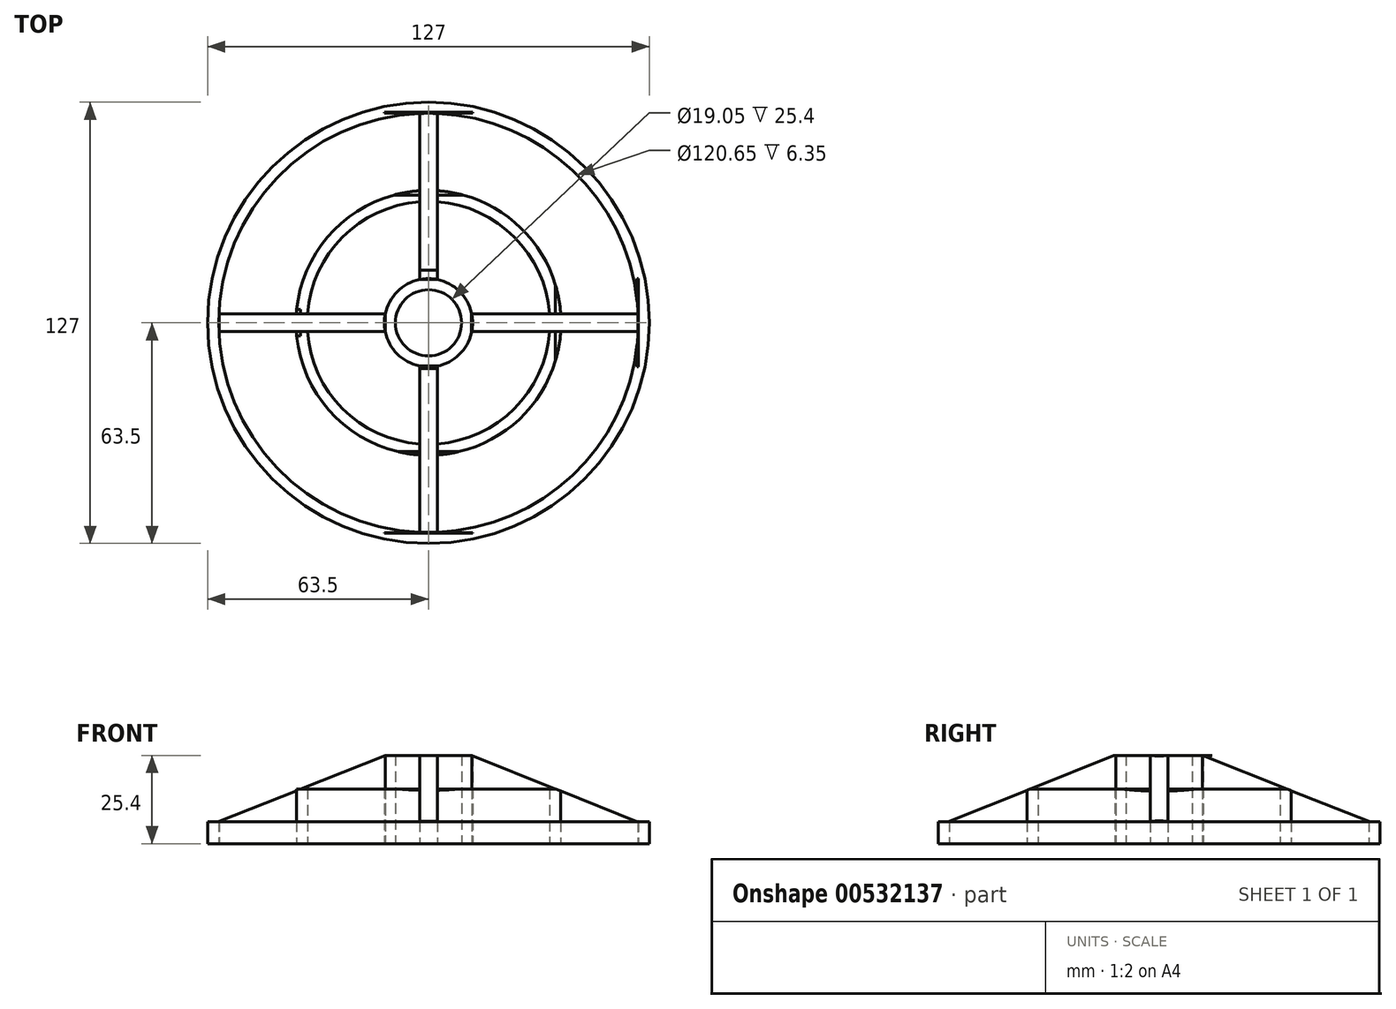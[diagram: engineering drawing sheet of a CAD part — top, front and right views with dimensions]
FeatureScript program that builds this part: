
annotation { "Feature Type Name" : "Feature", "Feature Type Description" : "" }
export const myFeature = defineFeature(function(context is Context, id is Id, definition is map)
    precondition{}
    {
        {
            var Q0;
            Q0=qCreatedBy(makeId("Top.planeOp"),FACE);
            var sketch = newSketch(context, id + "F0", { "sketchPlane" : qUnion([Q0])});
            skCircle(sketch, "E0", {"center": v(0, 0) * mm, "radius": 63.5 * mm});
            skCircle(sketch, "E1", {"center": v(0, 0) * mm, "radius": 38.1 * mm});
            skCircle(sketch, "E2", {"center": v(0, 0) * mm, "radius": 12.7 * mm});
            skLineSegment(sketch, "E3", {"start": v(-2.57, 63.45) * mm, "end": v(-2.57, 12.44) * mm});
            skLineSegment(sketch, "E4", {"start": v(2.51, 63.45) * mm, "end": v(2.51, 12.45) * mm});
            skLineSegment(sketch, "E5", {"start": v(-12.44, 2.55) * mm, "end": v(-63.45, 2.55) * mm});
            skLineSegment(sketch, "E6", {"start": v(-12.45, -2.53) * mm, "end": v(-63.45, -2.53) * mm});
            skLineSegment(sketch, "E7", {"start": v(2.51, -12.45) * mm, "end": v(2.51, -63.45) * mm});
            skLineSegment(sketch, "E8", {"start": v(-2.57, -12.44) * mm, "end": v(-2.57, -63.45) * mm});
            skLineSegment(sketch, "E9", {"start": v(12.44, 2.55) * mm, "end": v(63.45, 2.55) * mm});
            skLineSegment(sketch, "E10", {"start": v(12.45, -2.53) * mm, "end": v(63.45, -2.53) * mm});
            skCircle(sketch, "E11", {"center": v(0, 0) * mm, "radius": 60.33 * mm});
            skCircle(sketch, "E12", {"center": v(0, 0) * mm, "radius": 34.93 * mm});
            skCircle(sketch, "E13", {"center": v(0, 0) * mm, "radius": 9.53 * mm});
            skLineSegment(sketch, "E14", {"start": v(-60.21, 2.55) * mm, "end": v(-60.21, -2.53) * mm});
            skLineSegment(sketch, "E15", {"start": v(-12.44, 2.55) * mm, "end": v(-12.45, -2.53) * mm});
            skLineSegment(sketch, "E16", {"start": v(12.44, 2.55) * mm, "end": v(12.45, -2.53) * mm});
            skLineSegment(sketch, "E17", {"start": v(63.45, 2.55) * mm, "end": v(63.45, -2.53) * mm});
            skLineSegment(sketch, "E18", {"start": v(-2.57, 63.45) * mm, "end": v(2.51, 63.45) * mm});
            skLineSegment(sketch, "E19", {"start": v(2.51, 12.45) * mm, "end": v(-2.57, 12.44) * mm});
            skLineSegment(sketch, "E20", {"start": v(-2.57, -12.44) * mm, "end": v(2.51, -12.45) * mm});
            skLineSegment(sketch, "E21", {"start": v(2.51, -63.45) * mm, "end": v(-2.57, -63.45) * mm});
            skSolve(sketch);
        }
        {
            var Q0;
            Q0 = qSketchRegion(id + "F0", true);
            extrude(context, id + "F1", {"entities" : qUnion([Q0]), "depth" : 6.35 * mm, "offsetDistance" : 25.4 * mm});
        }
        {
            var Q0;
            {var subQ0=sQuery(id+"F0.wireOp",EDGE,"E3");var subQ1=sQuery(id+"F0.wireOp",EDGE,"E1");var subQ2=makeQuery(id+"F0.imprint","INTERSECT",VERTEX,{"derivedFrom":[subQ1,subQ0]});Q0=makeQuery(id+"F0.imprint","IMPRINT",FACE,{"disambiguationData":[TD([[makeQuery(id+"F0.imprint","IMPRINT",EDGE,{"disambiguationData":[TD([[subQ2,-1.0]])],"derivedFrom":subQ1}),1.0]])]});}
            var Q1;
            {var subQ0=sQuery(id+"F0.wireOp",EDGE,"E4");var subQ1=sQuery(id+"F0.wireOp",EDGE,"E1");var subQ2=makeQuery(id+"F0.imprint","INTERSECT",VERTEX,{"derivedFrom":[subQ1,subQ0]});Q1=makeQuery(id+"F0.imprint","IMPRINT",FACE,{"disambiguationData":[TD([[makeQuery(id+"F0.imprint","IMPRINT",EDGE,{"disambiguationData":[TD([[subQ2,1.0]])],"derivedFrom":subQ1}),1.0]])]});}
            var Q2;
            {var subQ0=sQuery(id+"F0.wireOp",EDGE,"E7");var subQ1=sQuery(id+"F0.wireOp",EDGE,"E1");var subQ2=makeQuery(id+"F0.imprint","INTERSECT",VERTEX,{"derivedFrom":[subQ1,subQ0]});Q2=makeQuery(id+"F0.imprint","IMPRINT",FACE,{"disambiguationData":[TD([[makeQuery(id+"F0.imprint","IMPRINT",EDGE,{"disambiguationData":[TD([[subQ2,-1.0]])],"derivedFrom":subQ1}),1.0]])]});}
            var Q3;
            {var subQ0=sQuery(id+"F0.wireOp",EDGE,"E6");var subQ1=sQuery(id+"F0.wireOp",EDGE,"E1");var subQ2=makeQuery(id+"F0.imprint","INTERSECT",VERTEX,{"derivedFrom":[subQ1,subQ0]});Q3=makeQuery(id+"F0.imprint","IMPRINT",FACE,{"disambiguationData":[TD([[makeQuery(id+"F0.imprint","IMPRINT",EDGE,{"disambiguationData":[TD([[subQ2,-1.0]])],"derivedFrom":subQ1}),1.0]])]});}
            extrude(context, id + "F2", {"entities" : qUnion([Q0, Q1, Q2, Q3]), "depth" : 15.75 * mm, "offsetDistance" : 25.4 * mm});
        }
        {
            var Q0;
            {var subQ5=sQuery(id+"F0.wireOp",EDGE,"E14");Q0=makeQuery(id+"F0.imprint","IMPRINT",FACE,{"disambiguationData":[TD([[makeQuery(id+"F0.imprint","IMPRINT",EDGE,{"derivedFrom":subQ5}),1.0]])]});}
            var Q1;
            {var subQ0=sQuery(id+"F0.wireOp",EDGE,"E5");var subQ1=sQuery(id+"F0.wireOp",EDGE,"E1");var subQ2=makeQuery(id+"F0.imprint","INTERSECT",VERTEX,{"derivedFrom":[subQ1,subQ0]});Q1=makeQuery(id+"F0.imprint","IMPRINT",FACE,{"disambiguationData":[TD([[makeQuery(id+"F0.imprint","IMPRINT",EDGE,{"disambiguationData":[TD([[subQ2,-1.0]])],"derivedFrom":subQ1}),1.0]])]});}
            var Q2;
            {var subQ1=sQuery(id+"F0.wireOp",EDGE,"E5");var subQ6=sQuery(id+"F0.wireOp",EDGE,"E12");var subQ7=makeQuery(id+"F0.imprint","INTERSECT",VERTEX,{"derivedFrom":[subQ1,subQ6]});Q2=makeQuery(id+"F0.imprint","IMPRINT",FACE,{"disambiguationData":[TD([[makeQuery(id+"F0.imprint","IMPRINT",EDGE,{"disambiguationData":[TD([[subQ7,-1.0]])],"derivedFrom":subQ6}),1.0]])]});}
            extrude(context, id + "F3", {"entities" : qUnion([Q0, Q1, Q2]), "depth" : 25.4 * mm, "offsetDistance" : 25.4 * mm});
        }
        {
            var Q0;
            Q0=makeQuery(id+"F0.imprint","IMPRINT",FACE,{"disambiguationData":[TD([[makeQuery(id+"F0.imprint","IMPRINT",EDGE,{"derivedFrom":sQuery(id+"F0.wireOp",EDGE,"E13")}),-1.0]])]});
            extrude(context, id + "F4", {"entities" : qUnion([Q0]), "depth" : 25.4 * mm, "offsetDistance" : 25.4 * mm});
        }
        {
            var Q0;
            {var subQ1=sQuery(id+"F0.wireOp",EDGE,"E3");var subQ6=sQuery(id+"F0.wireOp",EDGE,"E12");var subQ7=makeQuery(id+"F0.imprint","INTERSECT",VERTEX,{"derivedFrom":[subQ1,subQ6]});Q0=makeQuery(id+"F0.imprint","IMPRINT",FACE,{"disambiguationData":[TD([[makeQuery(id+"F0.imprint","IMPRINT",EDGE,{"disambiguationData":[TD([[subQ7,1.0]])],"derivedFrom":subQ6}),1.0]])]});}
            var Q1;
            {var subQ0=sQuery(id+"F0.wireOp",EDGE,"E4");var subQ1=sQuery(id+"F0.wireOp",EDGE,"E1");var subQ2=makeQuery(id+"F0.imprint","INTERSECT",VERTEX,{"derivedFrom":[subQ1,subQ0]});Q1=makeQuery(id+"F0.imprint","IMPRINT",FACE,{"disambiguationData":[TD([[makeQuery(id+"F0.imprint","IMPRINT",EDGE,{"disambiguationData":[TD([[subQ2,-1.0]])],"derivedFrom":subQ1}),1.0]])]});}
            var Q2;
            {var subQ0=sQuery(id+"F0.wireOp",EDGE,"E4");var subQ1=sQuery(id+"F0.wireOp",EDGE,"E1");var subQ2=makeQuery(id+"F0.imprint","INTERSECT",VERTEX,{"derivedFrom":[subQ1,subQ0]});Q2=makeQuery(id+"F0.imprint","IMPRINT",FACE,{"disambiguationData":[TD([[makeQuery(id+"F0.imprint","IMPRINT",EDGE,{"disambiguationData":[TD([[subQ2,-1.0]])],"derivedFrom":subQ1}),-1.0]])]});}
            extrude(context, id + "F5", {"entities" : qUnion([Q0, Q1, Q2]), "depth" : 25.4 * mm, "offsetDistance" : 25.4 * mm});
        }
        {
            var Q0;
            {var subQ1=sQuery(id+"F0.wireOp",EDGE,"E9");var subQ6=sQuery(id+"F0.wireOp",EDGE,"E12");var subQ7=makeQuery(id+"F0.imprint","INTERSECT",VERTEX,{"derivedFrom":[subQ1,subQ6]});Q0=makeQuery(id+"F0.imprint","IMPRINT",FACE,{"disambiguationData":[TD([[makeQuery(id+"F0.imprint","IMPRINT",EDGE,{"disambiguationData":[TD([[subQ7,1.0]])],"derivedFrom":subQ6}),1.0]])]});}
            var Q1;
            {var subQ0=sQuery(id+"F0.wireOp",EDGE,"E9");var subQ1=sQuery(id+"F0.wireOp",EDGE,"E1");var subQ2=makeQuery(id+"F0.imprint","INTERSECT",VERTEX,{"derivedFrom":[subQ1,subQ0]});Q1=makeQuery(id+"F0.imprint","IMPRINT",FACE,{"disambiguationData":[TD([[makeQuery(id+"F0.imprint","IMPRINT",EDGE,{"disambiguationData":[TD([[subQ2,1.0]])],"derivedFrom":subQ1}),1.0]])]});}
            var Q2;
            {var subQ0=sQuery(id+"F0.wireOp",EDGE,"E9");var subQ1=sQuery(id+"F0.wireOp",EDGE,"E1");var subQ2=makeQuery(id+"F0.imprint","INTERSECT",VERTEX,{"derivedFrom":[subQ1,subQ0]});Q2=makeQuery(id+"F0.imprint","IMPRINT",FACE,{"disambiguationData":[TD([[makeQuery(id+"F0.imprint","IMPRINT",EDGE,{"disambiguationData":[TD([[subQ2,1.0]])],"derivedFrom":subQ1}),-1.0]])]});}
            var Q3;
            {var subQ1=sQuery(id+"F0.wireOp",EDGE,"E7");var subQ6=sQuery(id+"F0.wireOp",EDGE,"E12");var subQ8=makeQuery(id+"F0.imprint","INTERSECT",VERTEX,{"derivedFrom":[subQ1,subQ6]});Q3=makeQuery(id+"F0.imprint","IMPRINT",FACE,{"disambiguationData":[TD([[makeQuery(id+"F0.imprint","IMPRINT",EDGE,{"disambiguationData":[TD([[subQ8,1.0]])],"derivedFrom":subQ6}),1.0]])]});}
            var Q4;
            {var subQ0=sQuery(id+"F0.wireOp",EDGE,"E8");var subQ1=sQuery(id+"F0.wireOp",EDGE,"E1");var subQ2=makeQuery(id+"F0.imprint","INTERSECT",VERTEX,{"derivedFrom":[subQ1,subQ0]});Q4=makeQuery(id+"F0.imprint","IMPRINT",FACE,{"disambiguationData":[TD([[makeQuery(id+"F0.imprint","IMPRINT",EDGE,{"disambiguationData":[TD([[subQ2,-1.0]])],"derivedFrom":subQ1}),1.0]])]});}
            var Q5;
            {var subQ0=sQuery(id+"F0.wireOp",EDGE,"E8");var subQ1=sQuery(id+"F0.wireOp",EDGE,"E1");var subQ2=makeQuery(id+"F0.imprint","INTERSECT",VERTEX,{"derivedFrom":[subQ1,subQ0]});Q5=makeQuery(id+"F0.imprint","IMPRINT",FACE,{"disambiguationData":[TD([[makeQuery(id+"F0.imprint","IMPRINT",EDGE,{"disambiguationData":[TD([[subQ2,-1.0]])],"derivedFrom":subQ1}),-1.0]])]});}
            extrude(context, id + "F6", {"entities" : qUnion([Q0, Q1, Q2, Q3, Q4, Q5]), "depth" : 25.4 * mm, "offsetDistance" : 25.4 * mm});
        }
        {
            var Q0;
            Q0=qCreatedBy(makeId("Front.planeOp"),FACE);
            var sketch = newSketch(context, id + "F7", { "sketchPlane" : qUnion([Q0])});
            skLineSegment(sketch, "E22", {"start": v(-60.26, 6.42) * mm, "end": v(-12.44, 25.4) * mm});
            skLineSegment(sketch, "E23", {"start": v(-12.44, 25.4) * mm, "end": v(-60.32, 25.4) * mm});
            skLineSegment(sketch, "E24", {"start": v(-60.32, 25.4) * mm, "end": v(-60.26, 6.42) * mm});
            skSolve(sketch);
        }
        {
            var Q0;
            Q0 = qSketchRegion(id + "F7", true);
            extrude(context, id + "F8", {"entities" : qUnion([Q0]), "operationType" : NewBodyOperationType.REMOVE, "endBound" : BoundingType.SYMMETRIC, "oppositeDirection" : true, "depth" : 7.62 * mm, "offsetDistance" : 25.4 * mm});
        }
        {
            var Q0;
            Q0=qCreatedBy(makeId("Right.planeOp"),FACE);
            var sketch = newSketch(context, id + "F9", { "sketchPlane" : qUnion([Q0])});
            skLineSegment(sketch, "E25", {"start": v(-12.14, 25.8) * mm, "end": v(-60.52, 6.3) * mm});
            skLineSegment(sketch, "E26", {"start": v(-60.52, 6.3) * mm, "end": v(-60.52, 26.22) * mm});
            skLineSegment(sketch, "E27", {"start": v(-60.52, 26.22) * mm, "end": v(-12.14, 25.8) * mm});
            skSolve(sketch);
        }
        {
            var Q0;
            Q0 = qSketchRegion(id + "F9", true);
            extrude(context, id + "F10", {"entities" : qUnion([Q0]), "operationType" : NewBodyOperationType.REMOVE, "endBound" : BoundingType.SYMMETRIC, "oppositeDirection" : true, "depth" : 25.4 * mm, "offsetDistance" : 25.4 * mm});
        }
        {
            var Q0;
            Q0=qCreatedBy(makeId("Right.planeOp"),FACE);
            var sketch = newSketch(context, id + "F11", { "sketchPlane" : qUnion([Q0])});
            skLineSegment(sketch, "E28", {"start": v(12.58, 25.38) * mm, "end": v(60.67, 6.24) * mm});
            skLineSegment(sketch, "E29", {"start": v(60.67, 6.24) * mm, "end": v(60.67, 25.8) * mm});
            skLineSegment(sketch, "E30", {"start": v(60.67, 25.8) * mm, "end": v(12.58, 25.38) * mm});
            skSolve(sketch);
        }
        {
            var Q0;
            Q0 = qSketchRegion(id + "F11", true);
            extrude(context, id + "F12", {"entities" : qUnion([Q0]), "operationType" : NewBodyOperationType.REMOVE, "endBound" : BoundingType.SYMMETRIC, "oppositeDirection" : true, "depth" : 25.4 * mm, "offsetDistance" : 25.4 * mm});
        }
        {
            var Q0;
            Q0=qCreatedBy(makeId("Front.planeOp"),FACE);
            var sketch = newSketch(context, id + "F13", { "sketchPlane" : qUnion([Q0])});
            skLineSegment(sketch, "E31", {"start": v(12.36, 25.4) * mm, "end": v(60.27, 6.25) * mm});
            skLineSegment(sketch, "E32", {"start": v(60.27, 25.66) * mm, "end": v(12.36, 25.4) * mm});
            skLineSegment(sketch, "E33", {"start": v(61.52, 12.59) * mm, "end": v(60.27, 6.25) * mm});
            skLineSegment(sketch, "E34", {"start": v(60.27, 25.66) * mm, "end": v(63.44, 24.97) * mm});
            skLineSegment(sketch, "E35", {"start": v(63.44, 24.97) * mm, "end": v(61.52, 12.59) * mm});
            skSolve(sketch);
        }
        {
            var Q0;
            Q0 = qSketchRegion(id + "F13", true);
            extrude(context, id + "F14", {"entities" : qUnion([Q0]), "operationType" : NewBodyOperationType.REMOVE, "endBound" : BoundingType.SYMMETRIC, "oppositeDirection" : true, "depth" : 25.4 * mm, "offsetDistance" : 25.4 * mm});
        }
    });
